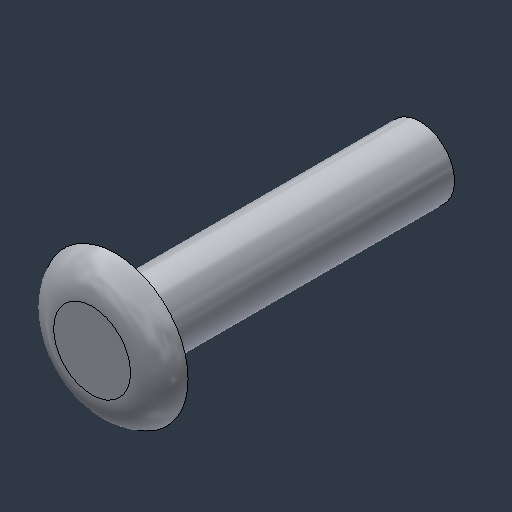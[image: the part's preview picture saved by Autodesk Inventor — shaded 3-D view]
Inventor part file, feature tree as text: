
AUTODESK INVENTOR PART (.ipt)
format: ipt  version: 2024.3 (Build 283343000, 343)  size: 116,736 bytes
history: native  units: mm (DEFAULTED — no unit token found)
features: fillet x1
ambient origin geometry x8: Origin, YZ Plane, XZ Plane, XY Plane, X Axis, Y Axis, Z Axis, Center Point
bodies: Solid1 (feature_tree)
feature tree (1):
  fillet  "Fillet1"  [1 undecoded]
note: 1 required parameter value undecoded (feature->parameter linkage not recoverable at this tier; creation-order binding heuristic only, values carry confidence <= 0.55)
